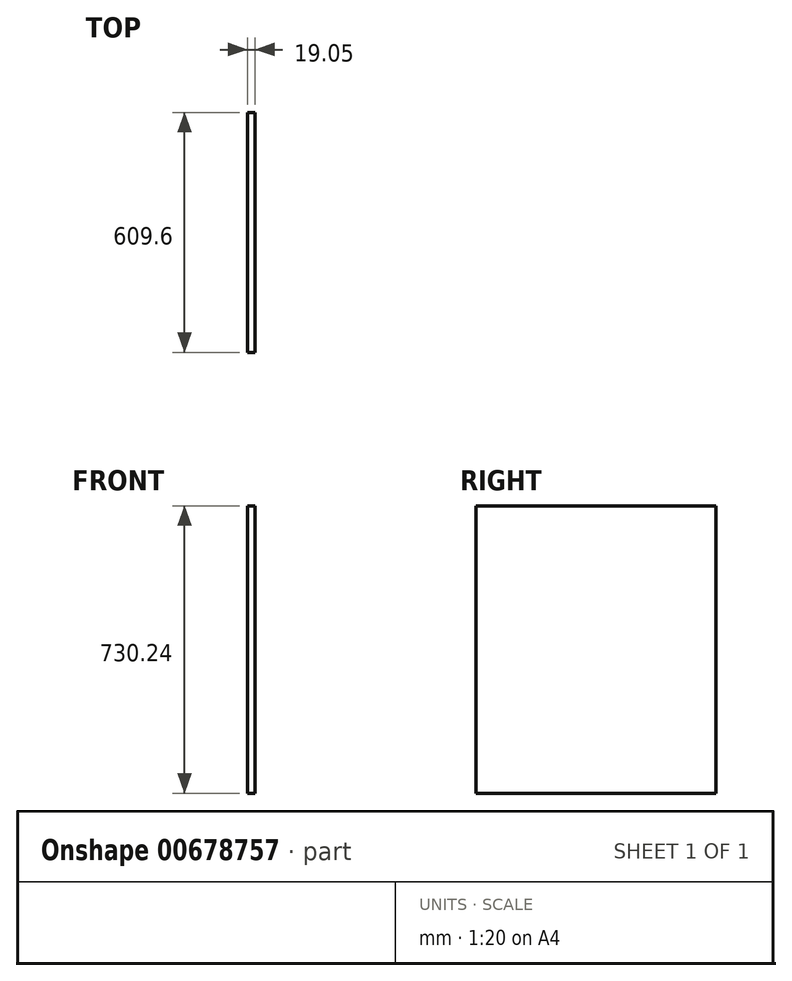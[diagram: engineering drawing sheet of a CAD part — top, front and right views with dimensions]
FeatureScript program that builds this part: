
annotation { "Feature Type Name" : "Feature", "Feature Type Description" : "" }
export const myFeature = defineFeature(function(context is Context, id is Id, definition is map)
    precondition{}
    {
        {
            var Q0;
            Q0=qCreatedBy(makeId("Right.planeOp"),FACE);
            var sketch = newSketch(context, id + "F0", { "sketchPlane" : qUnion([Q0])});
            skLineSegment(sketch, "E0.bottom", {"start": v(-304.8, 365.12) * mm, "end": v(304.8, 365.12) * mm});
            skLineSegment(sketch, "E0.top", {"start": v(-304.8, -365.13) * mm, "end": v(304.8, -365.13) * mm});
            skLineSegment(sketch, "E0.left", {"start": v(-304.8, 365.12) * mm, "end": v(-304.8, -365.13) * mm});
            skLineSegment(sketch, "E0.right", {"start": v(304.8, 365.12) * mm, "end": v(304.8, -365.13) * mm});
            skPoint(sketch, "E0.middle", {"position": v(0, 0) * mm});
            skSolve(sketch);
        }
        {
            var Q0;
            Q0=makeQuery(id+"F0.imprint","IMPRINT",FACE,{"disambiguationData":[TD([[makeQuery(id+"F0.imprint","IMPRINT",EDGE,{"derivedFrom":sQuery(id+"F0.wireOp",EDGE,"E0.bottom")}),-1.0]])]});
            extrude(context, id + "F1", {"entities" : qUnion([Q0]), "depth" : 19.05 * mm, "offsetDistance" : 25.4 * mm});
        }
    });
